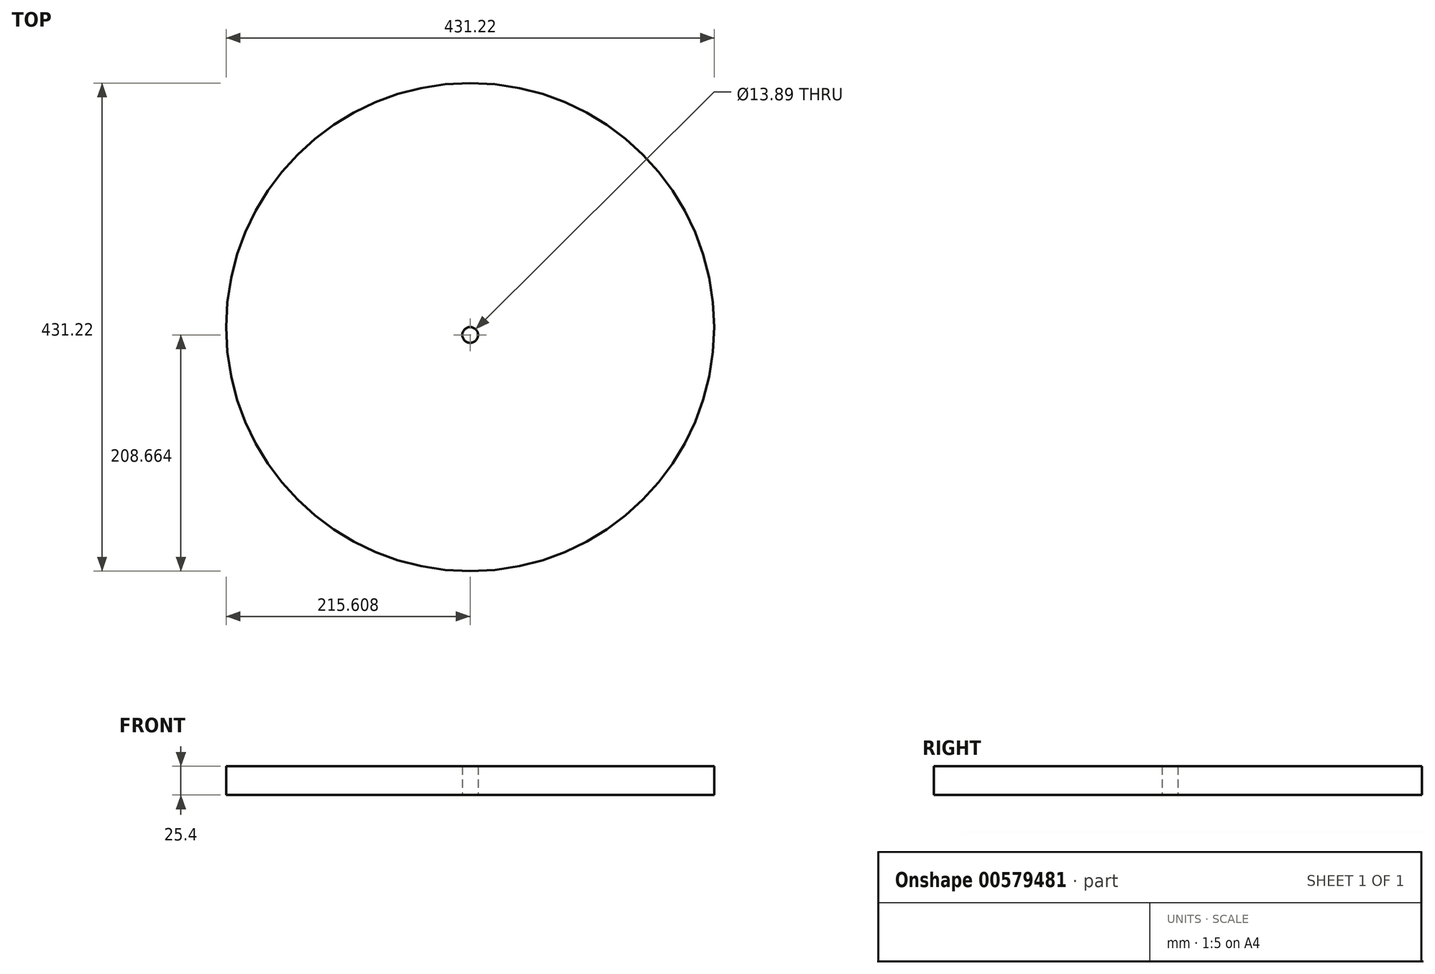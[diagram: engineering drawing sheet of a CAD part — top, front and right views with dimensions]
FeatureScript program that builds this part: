
annotation { "Feature Type Name" : "Feature", "Feature Type Description" : "" }
export const myFeature = defineFeature(function(context is Context, id is Id, definition is map)
    precondition{}
    {
        {
            var Q0;
            Q0=qCreatedBy(makeId("Top.planeOp"),FACE);
            var sketch = newSketch(context, id + "F0", { "sketchPlane" : qUnion([Q0])});
            skCircle(sketch, "E0", {"center": v(-23.65, -46.07) * mm, "radius": 6.94 * mm});
            skCircle(sketch, "E1", {"center": v(-23.65, -39.12) * mm, "radius": 215.6 * mm});
            skSolve(sketch);
        }
        {
            var Q0;
            Q0=makeQuery(id+"F0.imprint","IMPRINT",FACE,{"disambiguationData":[TD([[makeQuery(id+"F0.imprint","IMPRINT",EDGE,{"derivedFrom":sQuery(id+"F0.wireOp",EDGE,"E0")}),-1.0]])]});
            extrude(context, id + "F1", {"entities" : qUnion([Q0]), "depth" : 25.4 * mm, "offsetDistance" : 25.4 * mm});
        }
    });
